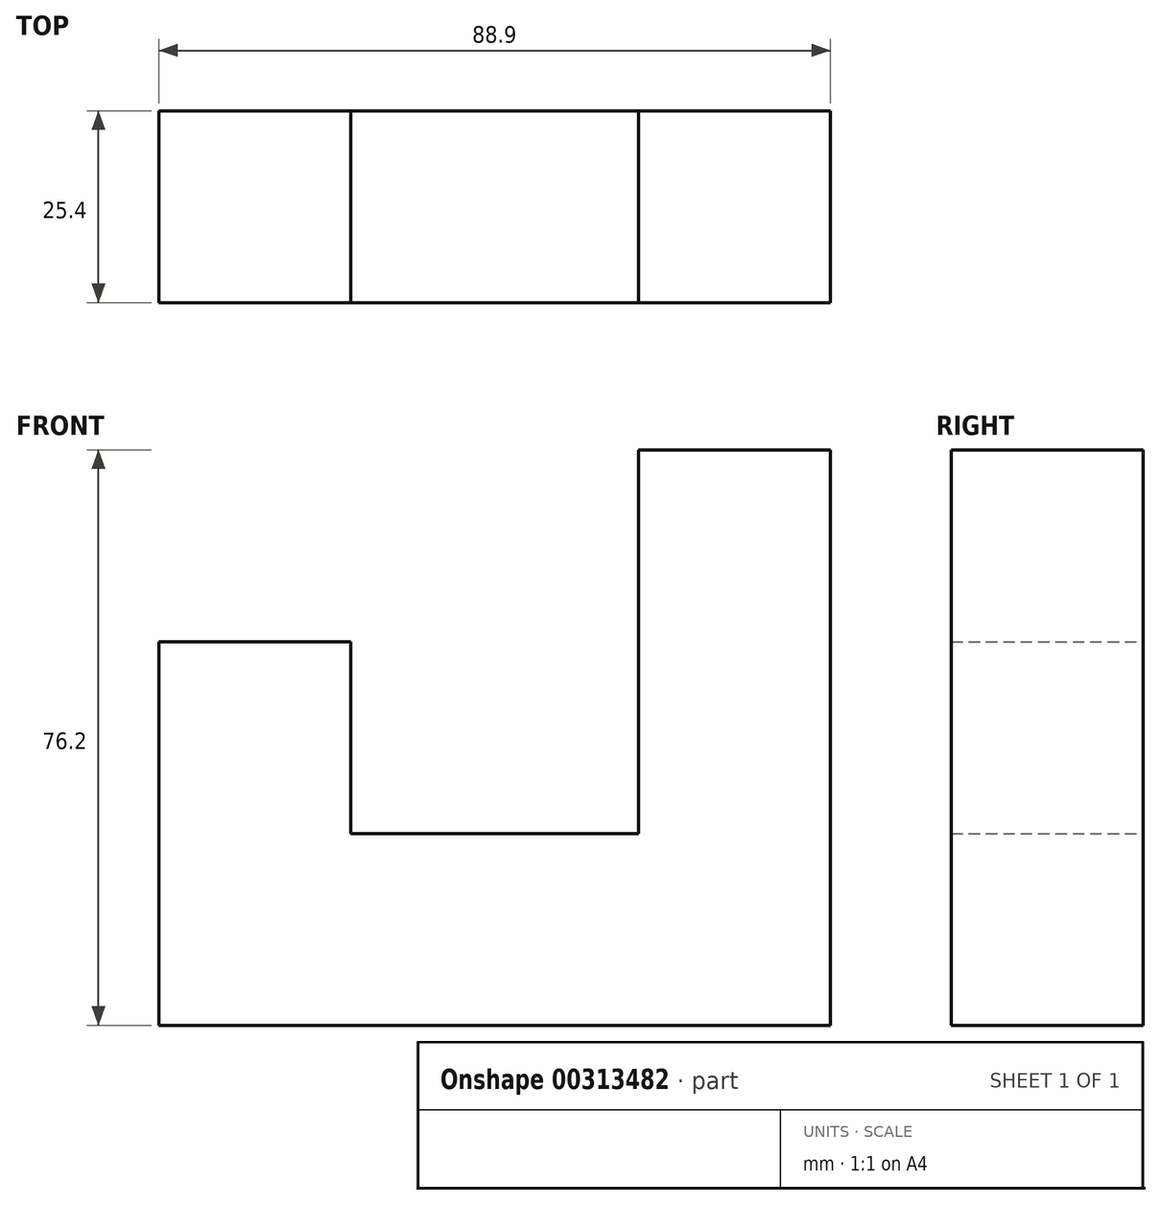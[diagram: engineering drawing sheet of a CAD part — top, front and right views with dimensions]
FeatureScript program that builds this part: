
annotation { "Feature Type Name" : "Feature", "Feature Type Description" : "" }
export const myFeature = defineFeature(function(context is Context, id is Id, definition is map)
    precondition{}
    {
        {
            var Q0;
            Q0=qCreatedBy(makeId("Front.planeOp"),FACE);
            var sketch = newSketch(context, id + "F0", { "sketchPlane" : qUnion([Q0])});
            skLineSegment(sketch, "E0", {"start": v(-28.2, 3.67) * mm, "end": v(-28.2, -47.13) * mm});
            skLineSegment(sketch, "E1", {"start": v(-28.2, -47.13) * mm, "end": v(60.7, -47.13) * mm});
            skLineSegment(sketch, "E2", {"start": v(60.7, -47.13) * mm, "end": v(60.7, 29.07) * mm});
            skLineSegment(sketch, "E3", {"start": v(60.7, 29.07) * mm, "end": v(35.3, 29.07) * mm});
            skLineSegment(sketch, "E4", {"start": v(35.3, 29.07) * mm, "end": v(35.3, -21.73) * mm});
            skLineSegment(sketch, "E5", {"start": v(35.3, -21.73) * mm, "end": v(-2.8, -21.73) * mm});
            skLineSegment(sketch, "E6", {"start": v(-2.8, -21.73) * mm, "end": v(-2.8, 3.67) * mm});
            skLineSegment(sketch, "E7", {"start": v(-2.8, 3.67) * mm, "end": v(-28.2, 3.67) * mm});
            skSolve(sketch);
        }
        {
            var Q0;
            Q0=makeQuery(id+"F0.imprint","IMPRINT",FACE,{"disambiguationData":[TD([[makeQuery(id+"F0.imprint","IMPRINT",EDGE,{"derivedFrom":sQuery(id+"F0.wireOp",EDGE,"E0")}),1.0]])]});
            extrude(context, id + "F1", {"entities" : qUnion([Q0]), "depth" : 25.4 * mm});
        }
    });
